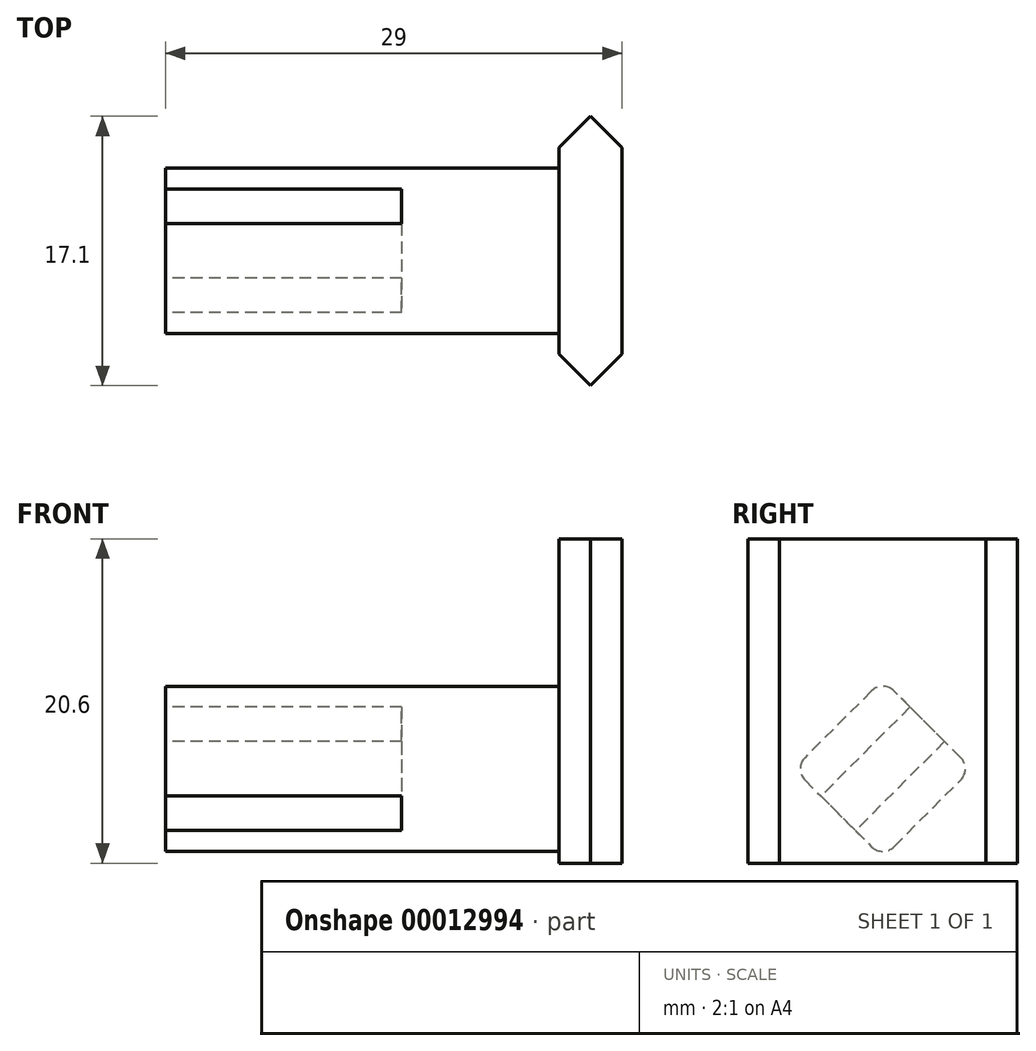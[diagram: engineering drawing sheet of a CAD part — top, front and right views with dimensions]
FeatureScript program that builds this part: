
annotation { "Feature Type Name" : "Feature", "Feature Type Description" : "" }
export const myFeature = defineFeature(function(context is Context, id is Id, definition is map)
    precondition{}
    {
        {
            var Q0;
            Q0=qCreatedBy(makeId("Right.planeOp"),FACE);
            var sketch = newSketch(context, id + "F0", { "sketchPlane" : qUnion([Q0])});
            skLineSegment(sketch, "E0", {"start": v(3.82, -10.3) * mm, "end": v(-3.82, -10.3) * mm, "construction": true});
            skLineSegment(sketch, "E1", {"start": v(-8.55, -5.57) * mm, "end": v(-8.55, 2.07) * mm, "construction": true});
            skLineSegment(sketch, "E2", {"start": v(-3.82, 8.55) * mm, "end": v(3.82, 8.55) * mm, "construction": true});
            skLineSegment(sketch, "E3", {"start": v(8.55, 3.82) * mm, "end": v(8.55, -3.82) * mm, "construction": true});
            skLineSegment(sketch, "E4.rect.bottom", {"start": v(-8.55, -10.3) * mm, "end": v(8.55, -10.3) * mm});
            skLineSegment(sketch, "E4.rect.top", {"start": v(-8.55, 10.3) * mm, "end": v(8.55, 10.3) * mm});
            skLineSegment(sketch, "E4.rect.left", {"start": v(-8.55, -10.3) * mm, "end": v(-8.55, 10.3) * mm});
            skLineSegment(sketch, "E4.rect.right", {"start": v(8.55, -10.3) * mm, "end": v(8.55, 10.3) * mm});
            skPoint(sketch, "E4.rect.middle", {"position": v(0, 0) * mm});
            skSolve(sketch);
        }
        {
            var Q0;
            Q0=makeQuery(id+"F0.imprint","IMPRINT",FACE,{"disambiguationData":[TD([[makeQuery(id+"F0.imprint","IMPRINT",EDGE,{"derivedFrom":sQuery(id+"F0.wireOp",EDGE,"E4.rect.bottom")}),1.0]])]});
            var Q1;
            Q1=sQuery(id+"F0.wireOp",EDGE,"101936be-83a2-4fce-959e-2ab3a7039490");
            var Q2;
            Q2=sQuery(id+"F0.wireOp",EDGE,"E0");
            var Q3;
            Q3=sQuery(id+"F0.wireOp",EDGE,"b89a5a71-419d-4db3-afde-2bc6dc5a35ce");
            var Q4;
            Q4=sQuery(id+"F0.wireOp",EDGE,"54915c50-2baa-4693-929c-c5879f3ac32b");
            var Q5;
            Q5=sQuery(id+"F0.wireOp",EDGE,"E1");
            var Q6;
            Q6=sQuery(id+"F0.wireOp",EDGE,"4ae48c00-830d-4c4e-b528-57efdb24ed3b");
            var Q7;
            Q7=sQuery(id+"F0.wireOp",EDGE,"ea53e517-876a-4359-9a04-de1147d445b5");
            var Q8;
            Q8=sQuery(id+"F0.wireOp",EDGE,"E2");
            var Q9;
            Q9=sQuery(id+"F0.wireOp",EDGE,"605ca1ea-edbc-4157-a758-2b93a1176bc0");
            var Q10;
            Q10=sQuery(id+"F0.wireOp",EDGE,"7ad1492e-fdff-4beb-a62a-381353a2cb63");
            var Q11;
            Q11=sQuery(id+"F0.wireOp",EDGE,"E3");
            var Q12;
            Q12=sQuery(id+"F0.wireOp",EDGE,"28caccf4-721c-4d13-a774-4335ff315007");
            extrude(context, id + "F1", {"entities" : qUnion([Q0]), "surfaceEntities" : qUnion([Q1, Q2, Q3, Q4, Q5, Q6, Q7, Q8, Q9, Q10, Q11, Q12]), "depth" : 4 * mm});
        }
        {
            var Q0;
            Q0=makeQuery(id+"F1.opExtrude","CAP_EDGE",EDGE,{"disambiguationData":[OSD([sQuery(id+"F0.wireOp",EDGE,"E4.rect.left")])],"isStart":true});
            var Q1;
            Q1=makeQuery(id+"F1.opExtrude","CAP_EDGE",EDGE,{"disambiguationData":[OSD([sQuery(id+"F0.wireOp",EDGE,"E4.rect.right")])],"isStart":true});
            var Q2;
            Q2=makeQuery(id+"F1.opExtrude","CAP_EDGE",EDGE,{"disambiguationData":[OSD([sQuery(id+"F0.wireOp",EDGE,"E4.rect.left")])],"isStart":false});
            var Q3;
            Q3=makeQuery(id+"F1.opExtrude","CAP_EDGE",EDGE,{"disambiguationData":[OSD([sQuery(id+"F0.wireOp",EDGE,"E4.rect.right")])],"isStart":false});
            chamfer(context, id + "F2", {"entities" : qUnion([Q0, Q1, Q2, Q3]), "width" : 2 * mm, "tangentPropagation" : true});
        }
        {
            var Q0;
            Q0=makeQuery(id+"F1.opExtrude","CAP_FACE",FACE,{"disambiguationData":[OSD([sQuery(id+"F0.wireOp",EDGE,"E4.rect.bottom"),sQuery(id+"F0.wireOp",EDGE,"E4.rect.top"),sQuery(id+"F0.wireOp",EDGE,"E4.rect.left"),sQuery(id+"F0.wireOp",EDGE,"E4.rect.right")])],"isStart":true});
            var sketch = newSketch(context, id + "F3", { "sketchPlane" : qUnion([Q0])});
            skPoint(sketch, "E5.0.midPoint", {"position": v(2.83, -2.83) * mm});
            skLineSegment(sketch, "E6", {"start": v(0, -10.3) * mm, "end": v(0, -4.3) * mm, "construction": true});
            skLineSegment(sketch, "E7", {"start": v(0, -4.3) * mm, "end": v(2.83, -1.47) * mm, "construction": true});
            skCircle(sketch, "E8.cCircle", {"center": v(0, -4.3) * mm, "radius": 4 * mm, "construction": true});
            skLineSegment(sketch, "E8.0", {"start": v(0, 1.36) * mm, "end": v(5.66, -4.3) * mm});
            skLineSegment(sketch, "E8.1", {"start": v(5.66, -4.3) * mm, "end": v(0, -9.96) * mm});
            skLineSegment(sketch, "E8.2", {"start": v(0, -9.96) * mm, "end": v(-5.66, -4.3) * mm});
            skLineSegment(sketch, "E8.3", {"start": v(-5.66, -4.3) * mm, "end": v(0, 1.36) * mm});
            skPoint(sketch, "E8.0.midPoint", {"position": v(2.83, -1.47) * mm});
            skSolve(sketch);
        }
        {
            var Q0;
            Q0 = qSketchRegion(id + "F3", true);
            extrude(context, id + "F4", {"entities" : qUnion([Q0]), "operationType" : NewBodyOperationType.ADD, "depth" : 25 * mm});
        }
        {
            var Q0;
            Q0=makeQuery(id+"F4.opExtrude","CAP_FACE",FACE,{"disambiguationData":[OSD([sQuery(id+"F3.wireOp",EDGE,"E8.0"),sQuery(id+"F3.wireOp",EDGE,"E8.1"),sQuery(id+"F3.wireOp",EDGE,"E8.2"),sQuery(id+"F3.wireOp",EDGE,"E8.3")])],"isStart":false});
            var sketch = newSketch(context, id + "F5", { "sketchPlane" : qUnion([Q0])});
            skLineSegment(sketch, "E9", {"start": v(-2.83, -7.13) * mm, "end": v(2.83, -1.47) * mm, "construction": true});
            skArc(sketch, "E10.0.startCap", {"start": v(-1.73, -8.22) * mm, "mid": v(-3.92, -8.22) * mm, "end": v(-3.92, -6.03) * mm, "construction": true});
            skArc(sketch, "E10.0.endCap", {"start": v(1.73, -0.38) * mm, "mid": v(3.92, -0.38) * mm, "end": v(3.92, -2.57) * mm, "construction": true});
            skLineSegment(sketch, "E10.0.left", {"start": v(-3.92, -6.03) * mm, "end": v(1.73, -0.38) * mm, "construction": true});
            skLineSegment(sketch, "E10.0.right", {"start": v(-1.73, -8.22) * mm, "end": v(3.92, -2.57) * mm, "construction": true});
            skLineSegment(sketch, "E11", {"start": v(-2.83, -1.47) * mm, "end": v(2.83, -7.13) * mm, "construction": true});
            skArc(sketch, "E12.0.startCap", {"start": v(-3.92, -2.57) * mm, "mid": v(-3.92, -0.38) * mm, "end": v(-1.73, -0.38) * mm});
            skArc(sketch, "E12.0.endCap", {"start": v(3.92, -6.03) * mm, "mid": v(3.92, -8.22) * mm, "end": v(1.73, -8.22) * mm});
            skLineSegment(sketch, "E12.0.left", {"start": v(-1.73, -0.38) * mm, "end": v(3.92, -6.03) * mm});
            skLineSegment(sketch, "E12.0.right", {"start": v(-3.92, -2.57) * mm, "end": v(1.73, -8.22) * mm});
            skSolve(sketch);
        }
        {
            var Q0;
            {var subQ2=sQuery(id+"F5.wireOp",EDGE,"E10.0.left");Q0=makeQuery(id+"F5.imprint","IMPRINT",FACE,{"disambiguationData":[TD([[makeQuery(id+"F5.imprint","IMPRINT",EDGE,{"derivedFrom":subQ2}),-1.0]])]});}
            var Q1;
            {var subQ0=sQuery(id+"F5.wireOp",EDGE,"E12.0.endCap");Q1=makeQuery(id+"F5.imprint","IMPRINT",FACE,{"disambiguationData":[TD([[makeQuery(id+"F5.imprint","IMPRINT",EDGE,{"derivedFrom":subQ0}),-1.0]])]});}
            var Q2;
            {var subQ0=sQuery(id+"F5.wireOp",EDGE,"E12.0.left");Q2=makeQuery(id+"F5.imprint","IMPRINT",FACE,{"disambiguationData":[TD([[makeQuery(id+"F5.imprint","IMPRINT",EDGE,{"derivedFrom":subQ0}),-1.0]])]});}
            var Q3;
            {var subQ0=sQuery(id+"F5.wireOp",EDGE,"E12.0.startCap");Q3=makeQuery(id+"F5.imprint","IMPRINT",FACE,{"disambiguationData":[TD([[makeQuery(id+"F5.imprint","IMPRINT",EDGE,{"derivedFrom":subQ0}),-1.0]])]});}
            extrude(context, id + "F6", {"entities" : qUnion([Q0, Q1, Q2, Q3]), "operationType" : NewBodyOperationType.REMOVE, "oppositeDirection" : true, "offsetDistance" : 25 * mm, "depth" : 15 * mm});
        }
        {
            var Q0;
            Q0=makeQuery(id+"F4.opExtrude","SWEPT_EDGE",EDGE,{"disambiguationData":[OSD([sQuery(id+"F3.wireOp",EDGE,"E8.1"),sQuery(id+"F3.wireOp",EDGE,"E8.2")])]});
            var Q1;
            Q1=makeQuery(id+"F4.opExtrude","SWEPT_EDGE",EDGE,{"disambiguationData":[OSD([sQuery(id+"F3.wireOp",EDGE,"E8.0"),sQuery(id+"F3.wireOp",EDGE,"E8.1")])]});
            var Q2;
            Q2=makeQuery(id+"F6.boolean.opBoolean","COPY",EDGE,{"derivedFrom":makeQuery(id+"F6.opExtrude","SWEPT_EDGE",EDGE,{"disambiguationData":[OSD([sQuery(id+"F3.wireOp",EDGE,"E8.1"),sQuery(id+"F5.wireOp",EDGE,"E12.0.endCap"),sQuery(id+"F5.wireOp",EDGE,"E12.0.left")])]})});
            var Q3;
            Q3=makeQuery(id+"F6.boolean.opBoolean","COPY",EDGE,{"derivedFrom":makeQuery(id+"F6.opExtrude","SWEPT_EDGE",EDGE,{"disambiguationData":[OSD([sQuery(id+"F3.wireOp",EDGE,"E8.1"),sQuery(id+"F5.wireOp",EDGE,"E12.0.endCap"),sQuery(id+"F5.wireOp",EDGE,"E12.0.right")])]})});
            var Q4;
            Q4=makeQuery(id+"F4.opExtrude","SWEPT_EDGE",EDGE,{"disambiguationData":[OSD([sQuery(id+"F3.wireOp",EDGE,"E8.2"),sQuery(id+"F3.wireOp",EDGE,"E8.3")])]});
            var Q5;
            Q5=makeQuery(id+"F6.boolean.opBoolean","COPY",EDGE,{"derivedFrom":makeQuery(id+"F6.opExtrude","SWEPT_EDGE",EDGE,{"disambiguationData":[OSD([sQuery(id+"F3.wireOp",EDGE,"E8.3"),sQuery(id+"F5.wireOp",EDGE,"E12.0.startCap"),sQuery(id+"F5.wireOp",EDGE,"E12.0.right")])]})});
            var Q6;
            Q6=makeQuery(id+"F6.boolean.opBoolean","COPY",EDGE,{"derivedFrom":makeQuery(id+"F6.opExtrude","SWEPT_EDGE",EDGE,{"disambiguationData":[OSD([sQuery(id+"F3.wireOp",EDGE,"E8.3"),sQuery(id+"F5.wireOp",EDGE,"E12.0.startCap"),sQuery(id+"F5.wireOp",EDGE,"E12.0.left")])]})});
            var Q7;
            Q7=makeQuery(id+"F4.opExtrude","SWEPT_EDGE",EDGE,{"disambiguationData":[OSD([sQuery(id+"F3.wireOp",EDGE,"E8.0"),sQuery(id+"F3.wireOp",EDGE,"E8.3")])]});
            fillet(context, id + "F7", {"entities" : qUnion([Q0, Q1, Q2, Q3, Q4, Q5, Q6, Q7]), "radius" : 1 * mm, "tangentPropagation" : true, "defaultsChanged" : false, "vertexSettings" : [], "allowEdgeOverflow" : false});
        }
    });
